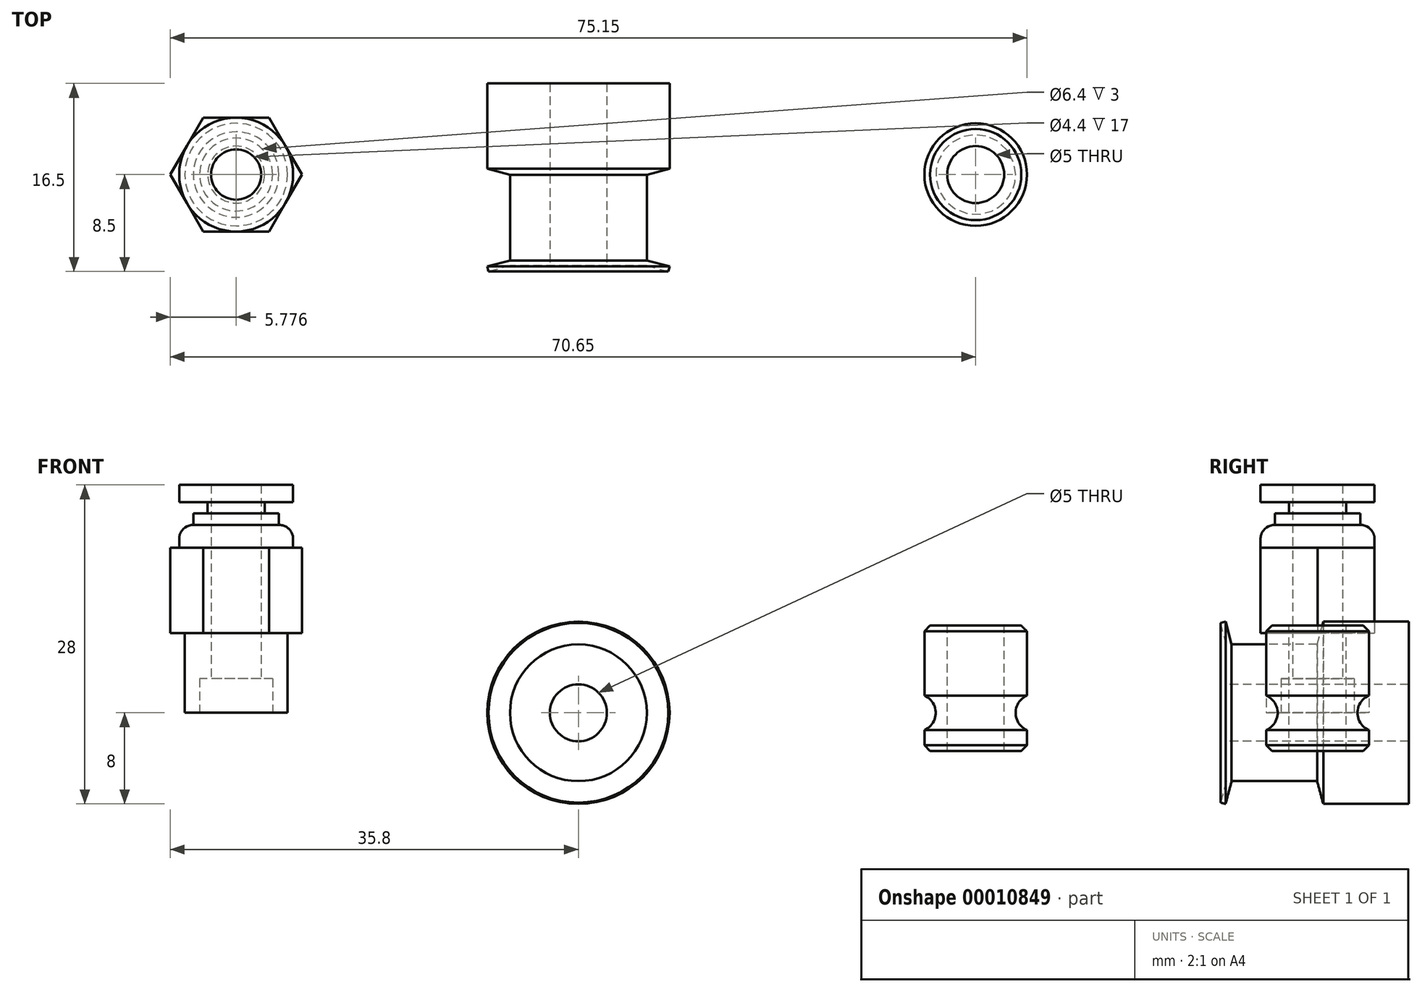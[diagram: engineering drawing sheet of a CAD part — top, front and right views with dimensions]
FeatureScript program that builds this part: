
annotation { "Feature Type Name" : "Feature", "Feature Type Description" : "" }
export const myFeature = defineFeature(function(context is Context, id is Id, definition is map)
    precondition{}
    {
        {
            var Q0;
            Q0=qCreatedBy(makeId("Right.planeOp"),FACE);
            var sketch = newSketch(context, id + "F0", { "sketchPlane" : qUnion([Q0])});
            skLineSegment(sketch, "E0", {"start": v(-20.69, 0) * mm, "end": v(25.26, 0) * mm, "construction": true});
            skLineSegment(sketch, "E1", {"start": v(-8, 0) * mm, "end": v(-8, 6) * mm});
            skLineSegment(sketch, "E2", {"start": v(-8, 6) * mm, "end": v(-8.5, 7.88) * mm});
            skLineSegment(sketch, "E3", {"start": v(-8.5, 7.88) * mm, "end": v(-8.07, 8) * mm});
            skLineSegment(sketch, "E4", {"start": v(-8.07, 8) * mm, "end": v(-7.54, 6) * mm});
            skLineSegment(sketch, "E5", {"start": v(-7.54, 6) * mm, "end": v(-0.04, 6) * mm});
            skLineSegment(sketch, "E6", {"start": v(-0.04, 6) * mm, "end": v(0.5, 8) * mm});
            skLineSegment(sketch, "E7", {"start": v(0.5, 8) * mm, "end": v(8, 8) * mm});
            skLineSegment(sketch, "E8", {"start": v(8, 8) * mm, "end": v(8, 0) * mm});
            skLineSegment(sketch, "E9", {"start": v(8, 0) * mm, "end": v(-8, 0) * mm});
            skLineSegment(sketch, "E10", {"start": v(-8, 2.5) * mm, "end": v(8, 2.5) * mm});
            skSolve(sketch);
        }
        {
            var Q0;
            {var subQ3=sQuery(id+"F0.wireOp",EDGE,"E2");Q0=makeQuery(id+"F0.imprint","IMPRINT",FACE,{"disambiguationData":[TD([[makeQuery(id+"F0.imprint","IMPRINT",EDGE,{"derivedFrom":subQ3}),-1.0]])]});}
            var Q1;
            Q1=sQuery(id+"F0.wireOp",EDGE,"E0");
            revolve(context, id + "F1", {"entities" : qUnion([Q0]), "axis" : qUnion([Q1]), "revolveType" : RevolveType.FULL});
        }
        {
            var Q0;
            Q0=qCreatedBy(makeId("Top.planeOp"),FACE);
            var sketch = newSketch(context, id + "F2", { "sketchPlane" : qUnion([Q0])});
            skCircle(sketch, "E11", {"center": v(-30.02, 0) * mm, "radius": 2.2 * mm});
            skCircle(sketch, "E12", {"center": v(-30.02, 0) * mm, "radius": 3.2 * mm});
            skCircle(sketch, "E13", {"center": v(-30.02, 0) * mm, "radius": 4.5 * mm});
            skSolve(sketch);
        }
        {
            var Q0;
            Q0=makeQuery(id+"F2.imprint","IMPRINT",FACE,{"disambiguationData":[TD([[makeQuery(id+"F2.imprint","IMPRINT",EDGE,{"derivedFrom":sQuery(id+"F2.wireOp",EDGE,"E12")}),-1.0]])]});
            extrude(context, id + "F3", {"entities" : qUnion([Q0]), "depth" : 3 * mm});
        }
        {
            var Q0;
            Q0=makeQuery(id+"F2.imprint","IMPRINT",FACE,{"disambiguationData":[TD([[makeQuery(id+"F2.imprint","IMPRINT",EDGE,{"derivedFrom":sQuery(id+"F2.wireOp",EDGE,"E11")}),-1.0]])]});
            extrude(context, id + "F4", {"entities" : qUnion([Q0]), "depth" : 7 * mm, "hasSecondDirection" : true, "secondDirectionOppositeDirection" : false, "secondDirectionDepth" : 3 * mm});
        }
        {
            var Q0;
            Q0=makeQuery(id+"F3.opExtrude","CAP_FACE",FACE,{"disambiguationData":[OSD([sQuery(id+"F2.wireOp",EDGE,"E12"),sQuery(id+"F2.wireOp",EDGE,"E13")])],"isStart":false});
            var Q1;
            Q1=makeQuery(id+"F4.opExtrude","CAP_FACE",FACE,{"disambiguationData":[OSD([sQuery(id+"F2.wireOp",EDGE,"E11"),sQuery(id+"F2.wireOp",EDGE,"E12")])],"isStart":false});
            extrude(context, id + "F5", {"entities" : qUnion([Q0]), "operationType" : NewBodyOperationType.ADD, "endBound" : BoundingType.UP_TO_SURFACE, "endBoundEntityFace" : qUnion([Q1]), "depth" : 25 * mm});
        }
        {
            var Q0;
            {var subQ0=sQuery(id+"F2.wireOp",EDGE,"E12");Q0=makeQuery(id+"F5.boolean.opBoolean","MERGE",FACE,{"derivedFrom":[makeQuery(id+"F4.opExtrude","CAP_FACE",FACE,{"disambiguationData":[OSD([sQuery(id+"F2.wireOp",EDGE,"E11"),subQ0])],"isStart":false}),makeQuery(id+"F5.opExtrude","CAP_FACE",FACE,{"disambiguationData":[OSD([subQ0,sQuery(id+"F2.wireOp",EDGE,"E13")])],"isStart":false})]});}
            var sketch = newSketch(context, id + "F6", { "sketchPlane" : qUnion([Q0])});
            skCircle(sketch, "E14.cCircle", {"center": v(-30.02, 0) * mm, "radius": 5 * mm, "construction": true});
            skLineSegment(sketch, "E14.0", {"start": v(-32.91, 5) * mm, "end": v(-27.14, 5) * mm});
            skLineSegment(sketch, "E14.1", {"start": v(-27.14, 5) * mm, "end": v(-24.25, 0) * mm});
            skLineSegment(sketch, "E14.2", {"start": v(-24.25, 0) * mm, "end": v(-27.14, -5) * mm});
            skLineSegment(sketch, "E14.3", {"start": v(-27.14, -5) * mm, "end": v(-32.91, -5) * mm});
            skLineSegment(sketch, "E14.4", {"start": v(-32.91, -5) * mm, "end": v(-35.8, 0) * mm});
            skLineSegment(sketch, "E14.5", {"start": v(-35.8, 0) * mm, "end": v(-32.91, 5) * mm});
            skPoint(sketch, "E14.0.midPoint", {"position": v(-30.02, 5) * mm});
            skSolve(sketch);
        }
        {
            var Q0;
            Q0=makeQuery(id+"F6.imprint","IMPRINT",FACE,{"disambiguationData":[TD([[makeQuery(id+"F6.imprint","IMPRINT",EDGE,{"derivedFrom":makeQuery(id+"F4.opExtrude","CAP_EDGE",EDGE,{"disambiguationData":[OSD([sQuery(id+"F2.wireOp",EDGE,"E11")])],"isStart":false})}),-1.0]])]});
            var Q1;
            Q1=makeQuery(id+"F6.imprint","IMPRINT",FACE,{"disambiguationData":[TD([[makeQuery(id+"F6.imprint","IMPRINT",EDGE,{"derivedFrom":sQuery(id+"F6.wireOp",EDGE,"E14.0")}),-1.0]])]});
            extrude(context, id + "F7", {"entities" : qUnion([Q0, Q1]), "operationType" : NewBodyOperationType.ADD, "depth" : 7.5 * mm});
        }
        {
            var Q0;
            Q0=makeQuery(id+"F7.opExtrude","CAP_FACE",FACE,{"disambiguationData":[OSD([sQuery(id+"F2.wireOp",EDGE,"E11"),sQuery(id+"F6.wireOp",EDGE,"E14.0"),sQuery(id+"F6.wireOp",EDGE,"E14.1"),sQuery(id+"F6.wireOp",EDGE,"E14.2"),sQuery(id+"F6.wireOp",EDGE,"E14.3"),sQuery(id+"F6.wireOp",EDGE,"E14.4"),sQuery(id+"F6.wireOp",EDGE,"E14.5")])],"isStart":false});
            var sketch = newSketch(context, id + "F8", { "sketchPlane" : qUnion([Q0])});
            skCircle(sketch, "E15", {"center": v(-30.02, 0) * mm, "radius": 5 * mm});
            skSolve(sketch);
        }
        {
            var Q0;
            Q0 = qSketchRegion(id + "F8", true);
            extrude(context, id + "F9", {"entities" : qUnion([Q0]), "operationType" : NewBodyOperationType.ADD, "depth" : 2 * mm});
        }
        {
            var Q0;
            Q0=makeQuery(id+"F9.opExtrude","CAP_EDGE",EDGE,{"disambiguationData":[OSD([sQuery(id+"F8.wireOp",EDGE,"E15")])],"isStart":false});
            fillet(context, id + "F10", {"entities" : qUnion([Q0]), "radius" : 1.25 * mm, "tangentPropagation" : true, "allowEdgeOverflow" : false});
        }
        {
            var Q0;
            Q0=makeQuery(id+"F9.opExtrude","CAP_FACE",FACE,{"disambiguationData":[OSD([sQuery(id+"F8.wireOp",EDGE,"E15")])],"isStart":false});
            extrude(context, id + "F11", {"entities" : qUnion([Q0]), "operationType" : NewBodyOperationType.ADD, "depth" : 1 * mm});
        }
        {
            var Q0;
            Q0=makeQuery(id+"F11.opExtrude","CAP_FACE",FACE,{"disambiguationData":[OSD([sQuery(id+"F8.wireOp",EDGE,"E15")])],"isStart":false});
            var sketch = newSketch(context, id + "F12", { "sketchPlane" : qUnion([Q0])});
            skCircle(sketch, "E16", {"center": v(-30.02, 0) * mm, "radius": 2.5 * mm});
            skSolve(sketch);
        }
        {
            var Q0;
            Q0=makeQuery(id+"F12.imprint","IMPRINT",FACE,{"disambiguationData":[TD([[makeQuery(id+"F12.imprint","IMPRINT",EDGE,{"derivedFrom":sQuery(id+"F12.wireOp",EDGE,"E16")}),1.0]])]});
            extrude(context, id + "F13", {"entities" : qUnion([Q0]), "operationType" : NewBodyOperationType.ADD, "depth" : 1 * mm});
        }
        {
            var Q0;
            Q0=makeQuery(id+"F13.opExtrude","CAP_FACE",FACE,{"disambiguationData":[OSD([sQuery(id+"F12.wireOp",EDGE,"E16")])],"isStart":false});
            var sketch = newSketch(context, id + "F14", { "sketchPlane" : qUnion([Q0])});
            skCircle(sketch, "E17", {"center": v(-30.02, 0) * mm, "radius": 5 * mm});
            skSolve(sketch);
        }
        {
            var Q0;
            Q0=makeQuery(id+"F14.imprint","IMPRINT",FACE,{"disambiguationData":[TD([[makeQuery(id+"F14.imprint","IMPRINT",EDGE,{"derivedFrom":sQuery(id+"F14.wireOp",EDGE,"E17")}),1.0]])]});
            var Q1;
            Q1=makeQuery(id+"F14.imprint","IMPRINT",FACE,{"disambiguationData":[TD([[makeQuery(id+"F14.imprint","IMPRINT",EDGE,{"derivedFrom":makeQuery(id+"F13.opExtrude","CAP_EDGE",EDGE,{"disambiguationData":[OSD([sQuery(id+"F12.wireOp",EDGE,"E16")])],"isStart":false})}),1.0]])]});
            extrude(context, id + "F15", {"entities" : qUnion([Q0, Q1]), "operationType" : NewBodyOperationType.ADD, "depth" : 1.5 * mm});
        }
        {
            var Q0;
            Q0=makeQuery(id+"F2.imprint","IMPRINT",FACE,{"disambiguationData":[TD([[makeQuery(id+"F2.imprint","IMPRINT",EDGE,{"derivedFrom":sQuery(id+"F2.wireOp",EDGE,"E11")}),1.0]])]});
            extrude(context, id + "F16", {"entities" : qUnion([Q0]), "operationType" : NewBodyOperationType.REMOVE, "endBound" : BoundingType.THROUGH_ALL, "depth" : 25 * mm});
        }
        {
            var Q0;
            Q0=qCreatedBy(makeId("Front.planeOp"),FACE);
            var sketch = newSketch(context, id + "F17", { "sketchPlane" : qUnion([Q0])});
            skLineSegment(sketch, "E18", {"start": v(34.85, 8.73) * mm, "end": v(34.85, -5.57) * mm, "construction": true});
            skLineSegment(sketch, "E19", {"start": v(34.85, 7.65) * mm, "end": v(38.85, 7.65) * mm});
            skLineSegment(sketch, "E20", {"start": v(38.85, 7.65) * mm, "end": v(39.35, 7.15) * mm});
            skLineSegment(sketch, "E21", {"start": v(39.35, 7.15) * mm, "end": v(39.35, 1.52) * mm});
            skLineSegment(sketch, "E22", {"start": v(34.85, -3.35) * mm, "end": v(38.85, -3.35) * mm});
            skLineSegment(sketch, "E23", {"start": v(38.85, -3.35) * mm, "end": v(39.35, -2.85) * mm});
            skLineSegment(sketch, "E24", {"start": v(39.35, -2.85) * mm, "end": v(39.35, -1.52) * mm});
            skLineSegment(sketch, "E25", {"start": v(37.35, 7.65) * mm, "end": v(37.35, -3.35) * mm});
            skArc(sketch, "E26", {"start": v(39.35, 1.52) * mm, "mid": v(38.35, 0) * mm, "end": v(39.35, -1.52) * mm});
            skSolve(sketch);
        }
        {
            var Q0;
            {var subQ3=sQuery(id+"F17.wireOp",EDGE,"E20");Q0=makeQuery(id+"F17.imprint","IMPRINT",FACE,{"disambiguationData":[TD([[makeQuery(id+"F17.imprint","IMPRINT",EDGE,{"derivedFrom":subQ3}),-1.0]])]});}
            var Q1;
            Q1=sQuery(id+"F17.wireOp",EDGE,"E18");
            revolve(context, id + "F18", {"entities" : qUnion([Q0]), "axis" : qUnion([Q1]), "revolveType" : RevolveType.FULL});
        }
    });
